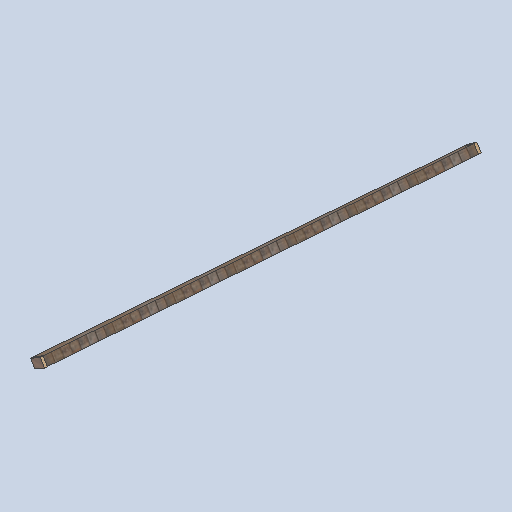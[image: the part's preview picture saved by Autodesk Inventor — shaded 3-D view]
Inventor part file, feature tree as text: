
AUTODESK INVENTOR PART (.ipt)
format: ipt  version: 2024.2 (Build 282272000, 272)  size: 310,272 bytes
history: native  units: mm
features: sketch x4, plane x2, extrude x2, projected_geometry x2, loft x1
ambient origin geometry x8: Origin, YZ Plane, XZ Plane, XY Plane, X Axis, Y Axis, Z Axis, Center Point
bodies: Solid1 (feature_tree)
feature tree (11):
  sketch  "Sketch1"  dims[d0=0.0mm d1=7900.0mm d2=0.0mm d3=90.0deg]
  plane  "Work Plane2"
  loft  "Loft1"
  sketch  "Sketch3"  dims[d8=50.0mm d9=0.0mm]
  sketch  "Sketch4"
  extrude  "Extrusion1"  Depth=50.0mm TaperAngle=0.0deg
  extrude  "Extrusion2"  [1 undecoded]
  plane  "Work Plane1"
  sketch  "Sketch2"  dims[d4=0.0mm d5=90.0deg d6=50.0mm d7=0.0mm]
  projected_geometry  "Projected Loop1"
  projected_geometry  "Projected Loop2"
note: 1 required parameter value undecoded (feature->parameter linkage not recoverable at this tier; creation-order binding heuristic only, values carry confidence <= 0.55)
